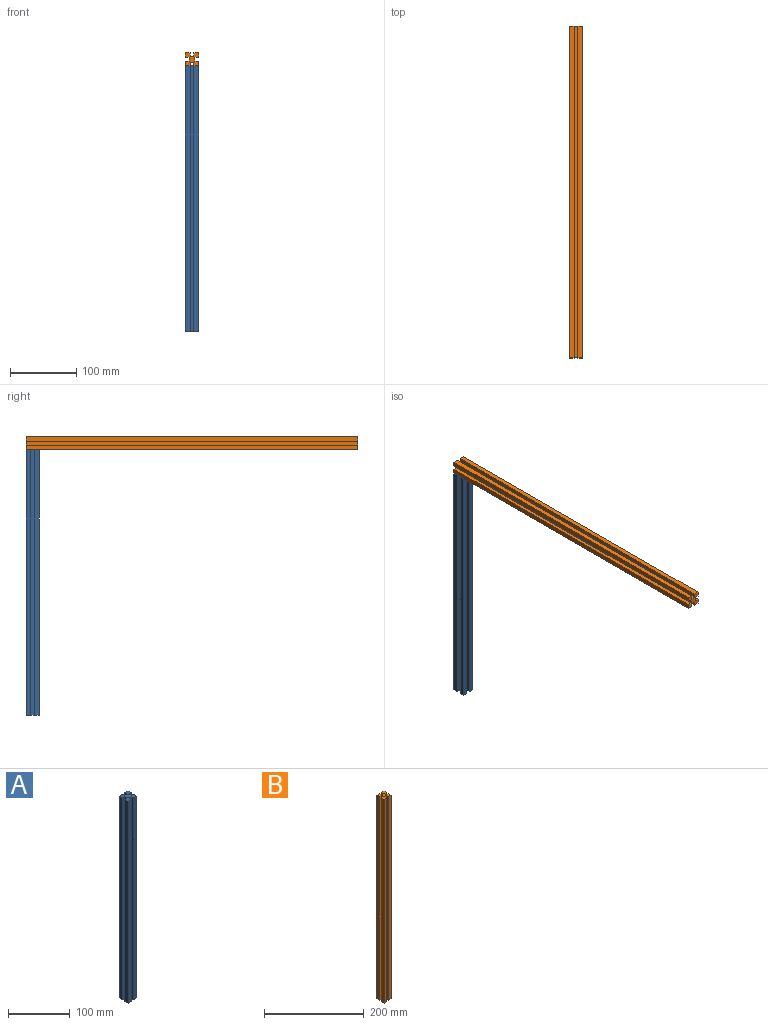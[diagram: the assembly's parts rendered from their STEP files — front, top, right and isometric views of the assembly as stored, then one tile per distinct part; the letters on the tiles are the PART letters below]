
ASSEMBLY  parts=2 mates=1
PART A: 22 faces, bbox 20x20x400 mm
  f0: plane 400x7mm, normal (-1,0,0), area 2800mm2, adj f1,f19,f20,f21
  f1: plane 400x7mm, normal (0,-1,0), area 2800mm2, adj f0,f2,f20,f21
  f2: plane 400x5.5mm, normal (1,0,0), area 2200mm2, adj f1,f3,f20,f21
  f3: plane 400x6mm, normal (0,-1,0), area 2400mm2, adj f2,f4,f20,f21
  f4: plane 400x5.5mm, normal (-1,0,0), area 2200mm2, adj f3,f5,f20,f21
  f5: plane 400x7mm, normal (0,-1,0), area 2800mm2, adj f4,f6,f20,f21
  f6: plane 400x7mm, normal (1,0,0), area 2800mm2, adj f5,f7,f20,f21
  f7: plane 400x5.5mm, normal (0,1,0), area 2200mm2, adj f6,f8,f20,f21
  f8: plane 400x6mm, normal (1,0,0), area 2400mm2, adj f7,f9,f20,f21
  f9: plane 400x5.5mm, normal (0,-1,0), area 2200mm2, adj f8,f10,f20,f21
  f10: plane 400x7mm, normal (1,0,0), area 2800mm2, adj f9,f11,f20,f21
  f11: plane 400x7mm, normal (0,1,0), area 2800mm2, adj f10,f12,f20,f21
  f12: plane 400x5.5mm, normal (-1,0,0), area 2200mm2, adj f11,f13,f20,f21
  f13: plane 400x6mm, normal (0,1,0), area 2400mm2, adj f12,f14,f20,f21
  f14: plane 400x5.5mm, normal (1,0,0), area 2200mm2, adj f13,f15,f20,f21
  f15: plane 400x7mm, normal (0,1,0), area 2800mm2, adj f14,f16,f20,f21
  f16: plane 400x7mm, normal (-1,0,0), area 2800mm2, adj f15,f17,f20,f21
  f17: plane 400x5.5mm, normal (0,-1,0), area 2200mm2, adj f16,f18,f20,f21
  f18: plane 400x6mm, normal (-1,0,0), area 2400mm2, adj f17,f19,f20,f21
  f19: plane 400x5.5mm, normal (0,1,0), area 2200mm2, adj f0,f18,f20,f21
  f20: plane 20x20mm, normal (0,0,1), area 268mm2, adj f0,f1,f2,f3,f4,f5,f6,f7
  f21: plane 20x20mm, normal (0,0,-1), area 268mm2, adj f0,f1,f2,f3,f4,f5,f6,f7
PART B: 22 faces, bbox 20x20x500 mm
  f0: plane 500x7mm, normal (-1,0,0), area 3500mm2, adj f1,f19,f20,f21
  f1: plane 500x7mm, normal (0,-1,0), area 3500mm2, adj f0,f2,f20,f21
  f2: plane 500x5.5mm, normal (1,0,0), area 2750mm2, adj f1,f3,f20,f21
  f3: plane 500x6mm, normal (0,-1,0), area 3000mm2, adj f2,f4,f20,f21
  f4: plane 500x5.5mm, normal (-1,0,0), area 2750mm2, adj f3,f5,f20,f21
  f5: plane 500x7mm, normal (0,-1,0), area 3500mm2, adj f4,f6,f20,f21
  f6: plane 500x7mm, normal (1,0,0), area 3500mm2, adj f5,f7,f20,f21
  f7: plane 500x5.5mm, normal (0,1,0), area 2750mm2, adj f6,f8,f20,f21
  f8: plane 500x6mm, normal (1,0,0), area 3000mm2, adj f7,f9,f20,f21
  f9: plane 500x5.5mm, normal (0,-1,0), area 2750mm2, adj f8,f10,f20,f21
  f10: plane 500x7mm, normal (1,0,0), area 3500mm2, adj f9,f11,f20,f21
  f11: plane 500x7mm, normal (0,1,0), area 3500mm2, adj f10,f12,f20,f21
  f12: plane 500x5.5mm, normal (-1,0,0), area 2750mm2, adj f11,f13,f20,f21
  f13: plane 500x6mm, normal (0,1,0), area 3000mm2, adj f12,f14,f20,f21
  f14: plane 500x5.5mm, normal (1,0,0), area 2750mm2, adj f13,f15,f20,f21
  f15: plane 500x7mm, normal (0,1,0), area 3500mm2, adj f14,f16,f20,f21
  f16: plane 500x7mm, normal (-1,0,0), area 3500mm2, adj f15,f17,f20,f21
  f17: plane 500x5.5mm, normal (0,-1,0), area 2750mm2, adj f16,f18,f20,f21
  f18: plane 500x6mm, normal (-1,0,0), area 3000mm2, adj f17,f19,f20,f21
  f19: plane 500x5.5mm, normal (0,1,0), area 2750mm2, adj f0,f18,f20,f21
  f20: plane 20x20mm, normal (0,0,1), area 268mm2, adj f0,f1,f2,f3,f4,f5,f6,f7
  f21: plane 20x20mm, normal (0,0,-1), area 268mm2, adj f0,f1,f2,f3,f4,f5,f6,f7
PLACE A rot(axis=(0,0,1),90deg) t=(-250,-16.5,20)mm
PLACE B rot(axis=(0,-0.71,0.71),180deg) t=(-250,3.5,440)mm
MATE fastened A.f20 <-> B.f11  axis (0,0,1) through (-270,3.5,420)mm
